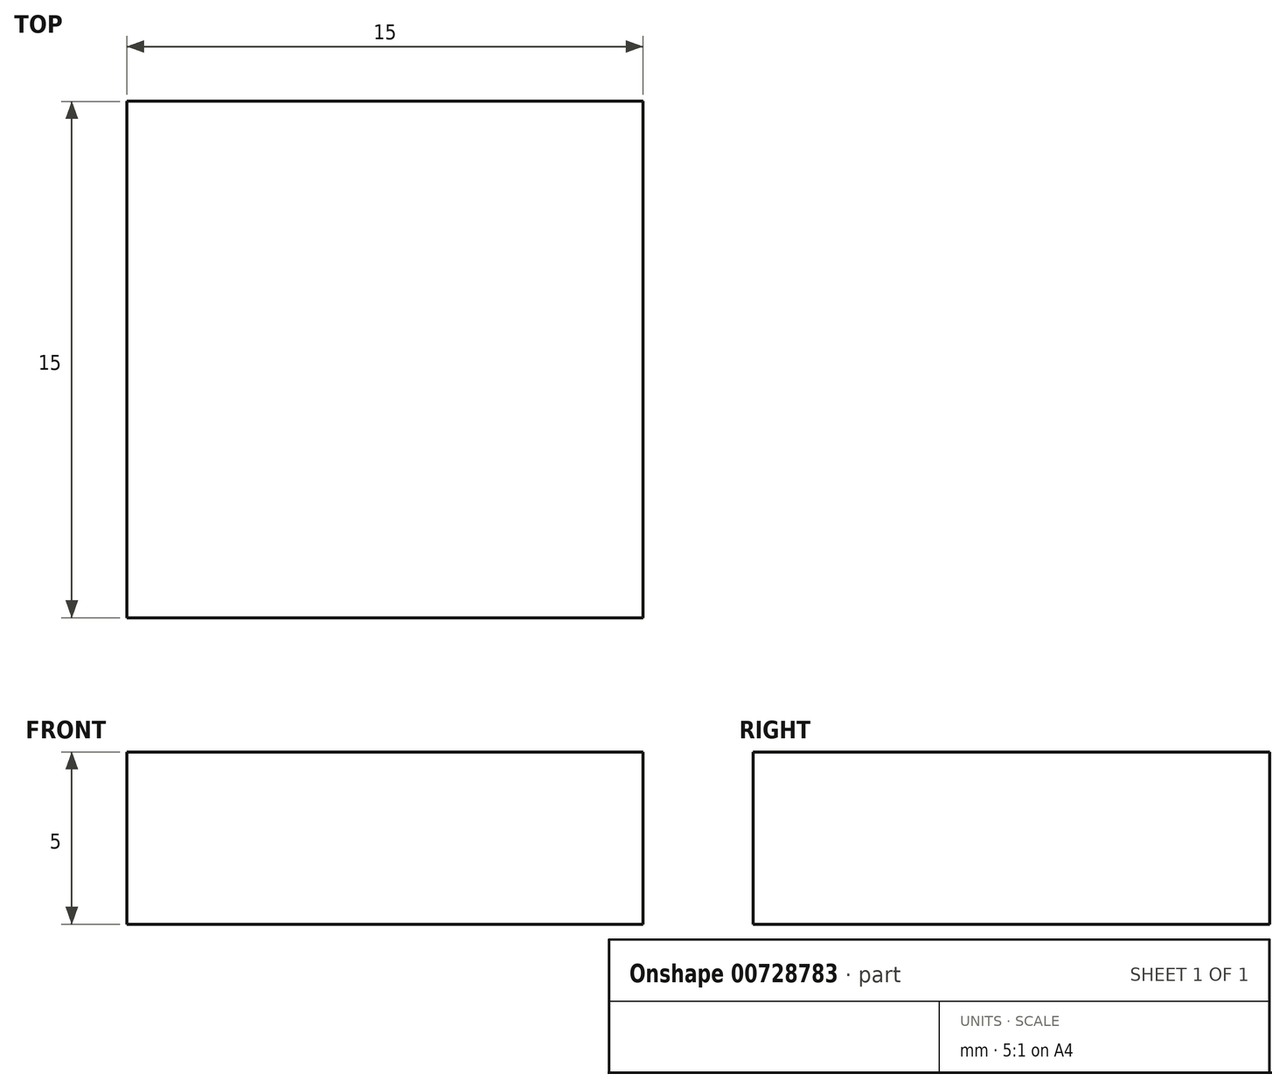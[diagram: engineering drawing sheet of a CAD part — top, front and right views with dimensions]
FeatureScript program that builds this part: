
annotation { "Feature Type Name" : "Feature", "Feature Type Description" : "" }
export const myFeature = defineFeature(function(context is Context, id is Id, definition is map)
    precondition{}
    {
        {
            var Q0;
            Q0=qCreatedBy(makeId("Top.planeOp"),FACE);
            var sketch = newSketch(context, id + "F0", { "sketchPlane" : qUnion([Q0])});
            skLineSegment(sketch, "E0.bottom", {"start": v(-15, 6.61) * mm, "end": v(0, 6.61) * mm});
            skLineSegment(sketch, "E0.top", {"start": v(-15, -8.39) * mm, "end": v(0, -8.39) * mm});
            skLineSegment(sketch, "E0.left", {"start": v(-15, 6.61) * mm, "end": v(-15, -8.39) * mm});
            skLineSegment(sketch, "E0.right", {"start": v(0, 6.61) * mm, "end": v(0, -8.39) * mm});
            skSolve(sketch);
        }
        {
            var Q0;
            Q0 = qSketchRegion(id + "F0", true);
            extrude(context, id + "F1", {"entities" : qUnion([Q0]), "depth" : 5 * mm, "offsetDistance" : 25 * mm});
        }
    });
